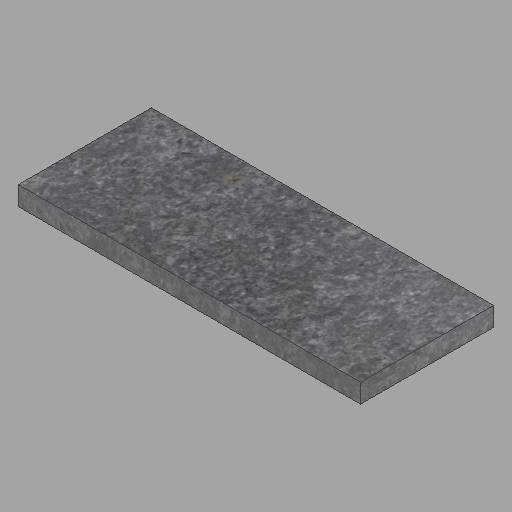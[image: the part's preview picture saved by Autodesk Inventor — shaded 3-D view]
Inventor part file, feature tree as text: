
AUTODESK INVENTOR PART (.ipt)
format: ipt  version: 2023 (Build 270158000, 158)  size: 221,696 bytes
history: native  units: in
note: dims shown in document units (in); Inventor stores cm internally (conversion verified against a paired STEP export)
features: other x1, extrude x1, sketch x1
ambient origin geometry x8: Origin, YZ Plane, XZ Plane, XY Plane, X Axis, Y Axis, Z Axis, Center Point
bodies: Solid1 (feature_tree)
feature tree (3):
  other  "2x14x36-4"
  extrude  "Extrusion1"  Depth=14.0in
  sketch  "Sketch1"  dims[d0=2.0in d1=14.0in d2=36.0in d3=0.0in]
